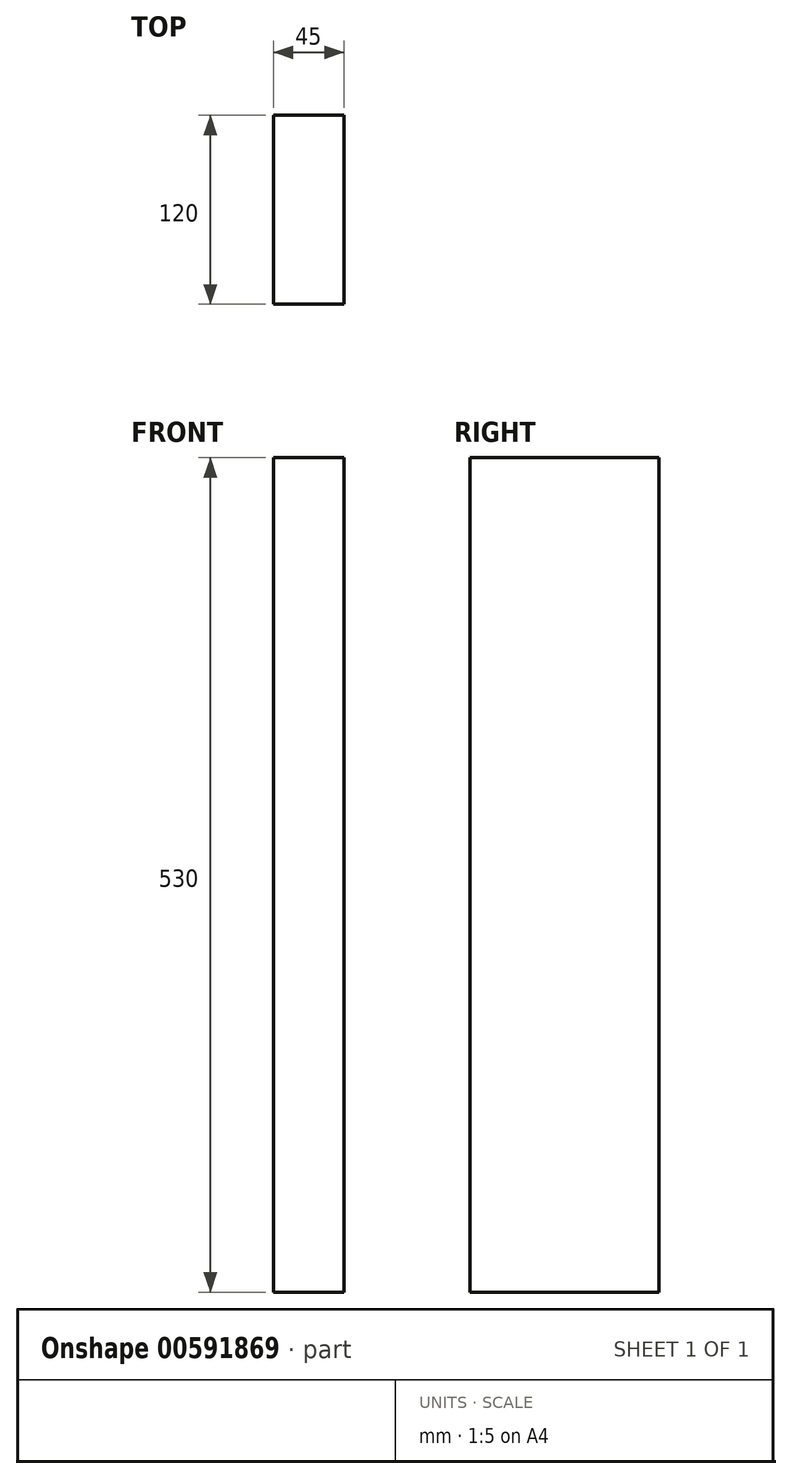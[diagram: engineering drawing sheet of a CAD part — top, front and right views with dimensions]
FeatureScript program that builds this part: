
annotation { "Feature Type Name" : "Feature", "Feature Type Description" : "" }
export const myFeature = defineFeature(function(context is Context, id is Id, definition is map)
    precondition{}
    {
        {
            var Q0;
            Q0=qCreatedBy(makeId("Top.planeOp"),FACE);
            var sketch = newSketch(context, id + "F0", { "sketchPlane" : qUnion([Q0])});
            skLineSegment(sketch, "E0.bottom", {"start": v(0, 0) * mm, "end": v(45, 0) * mm});
            skLineSegment(sketch, "E0.top", {"start": v(0, 120) * mm, "end": v(45, 120) * mm});
            skLineSegment(sketch, "E0.left", {"start": v(0, 0) * mm, "end": v(0, 120) * mm});
            skLineSegment(sketch, "E0.right", {"start": v(45, 0) * mm, "end": v(45, 120) * mm});
            skSolve(sketch);
        }
        {
            var Q0;
            Q0=makeQuery(id+"F0.imprint","IMPRINT",FACE,{"disambiguationData":[TD([[makeQuery(id+"F0.imprint","IMPRINT",EDGE,{"derivedFrom":sQuery(id+"F0.wireOp",EDGE,"E0.bottom")}),1.0]])]});
            extrude(context, id + "F1", {"entities" : qUnion([Q0]), "depth" : 530 * mm, "offsetDistance" : 25 * mm});
        }
    });
